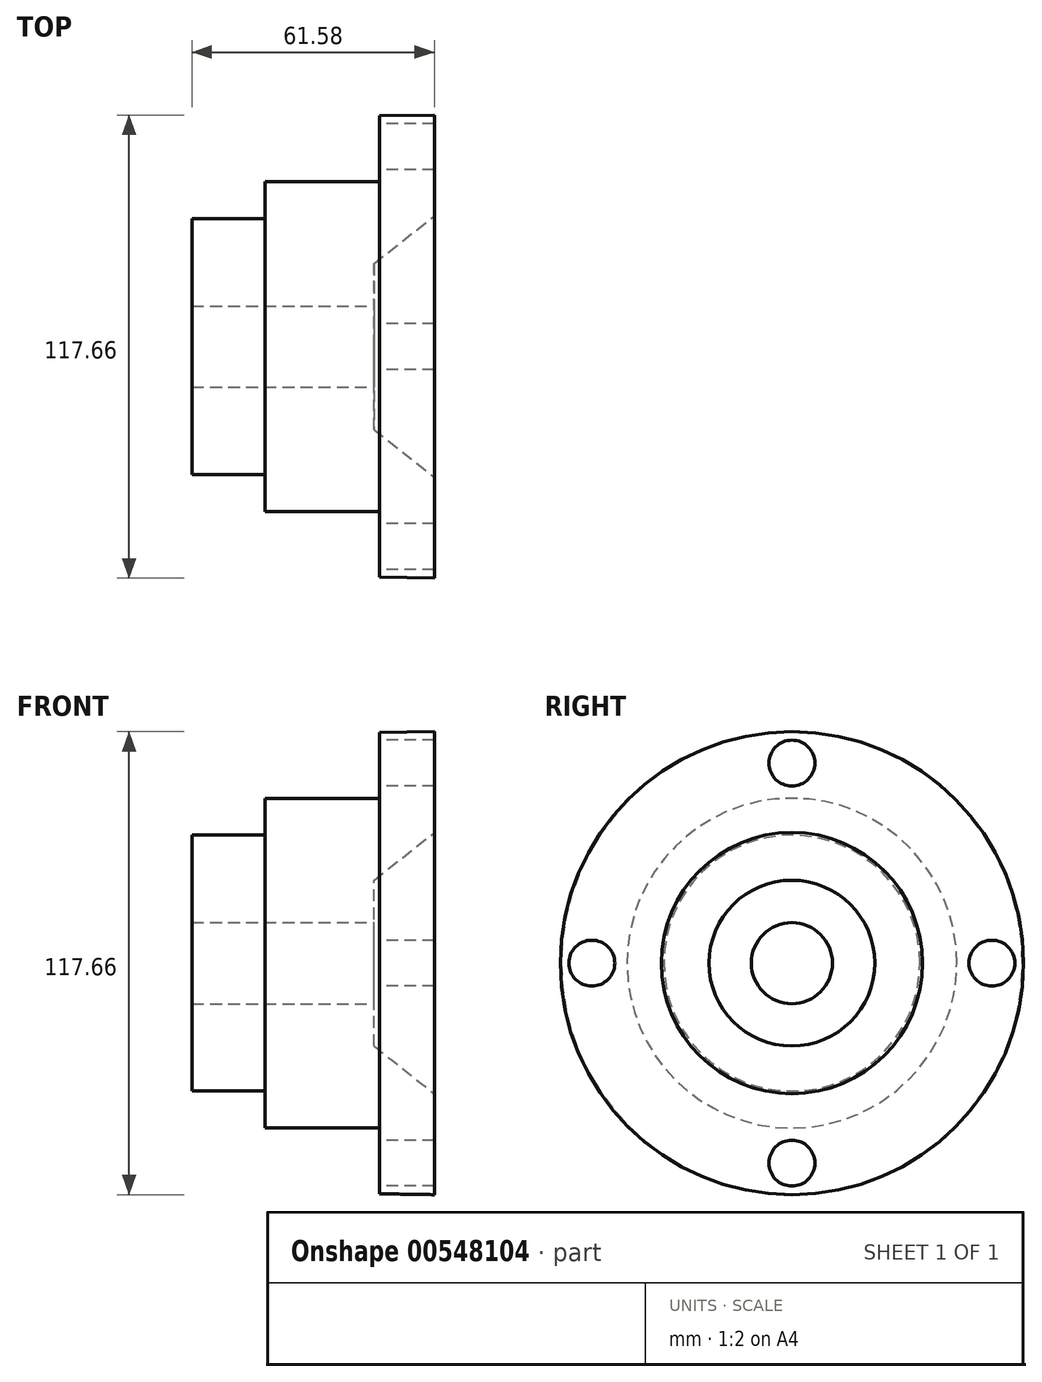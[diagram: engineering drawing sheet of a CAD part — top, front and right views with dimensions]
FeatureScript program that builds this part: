
annotation { "Feature Type Name" : "Feature", "Feature Type Description" : "" }
export const myFeature = defineFeature(function(context is Context, id is Id, definition is map)
    precondition{}
    {
        {
            var Q0;
            Q0=qCreatedBy(makeId("Front.planeOp"),FACE);
            var sketch = newSketch(context, id + "F0", { "sketchPlane" : qUnion([Q0])});
            skLineSegment(sketch, "E0", {"start": v(24.04, 58.83) * mm, "end": v(24.04, 33.2) * mm});
            skLineSegment(sketch, "E1", {"start": v(24.04, 33.2) * mm, "end": v(8.7, 21.06) * mm});
            skLineSegment(sketch, "E2", {"start": v(8.7, 21.06) * mm, "end": v(8.7, 10.3) * mm});
            skLineSegment(sketch, "E3", {"start": v(8.7, 10.3) * mm, "end": v(-37.54, 10.3) * mm});
            skLineSegment(sketch, "E4", {"start": v(-37.54, 10.3) * mm, "end": v(-37.54, 32.5) * mm});
            skLineSegment(sketch, "E5", {"start": v(-37.54, 32.5) * mm, "end": v(-19, 32.5) * mm});
            skLineSegment(sketch, "E6", {"start": v(-19, 32.5) * mm, "end": v(-19, 41.9) * mm});
            skLineSegment(sketch, "E7", {"start": v(-19, 41.9) * mm, "end": v(10.07, 41.9) * mm});
            skLineSegment(sketch, "E8", {"start": v(10.07, 41.9) * mm, "end": v(10.07, 58.6) * mm});
            skLineSegment(sketch, "E9", {"start": v(10.07, 58.6) * mm, "end": v(24.04, 58.83) * mm});
            skLineSegment(sketch, "E10", {"start": v(0, 0) * mm, "end": v(-77.83, 0) * mm});
            skSolve(sketch);
        }
        {
            var Q0;
            Q0 = qSketchRegion(id + "F0", true);
            var Q1;
            Q1=sQuery(id+"F0.wireOp",EDGE,"E10");
            revolve(context, id + "F1", {"entities" : qUnion([Q0]), "axis" : qUnion([Q1]), "revolveType" : RevolveType.FULL});
        }
        {
            var Q0;
            Q0=makeQuery(id+"F1.opRevolve","SWEPT_FACE",FACE,{"disambiguationData":[OSD([sQuery(id+"F0.wireOp",EDGE,"E8")])]});
            var sketch = newSketch(context, id + "F2", { "sketchPlane" : qUnion([Q0])});
            skLineSegment(sketch, "E11", {"start": v(0, 0) * mm, "end": v(0, 71.2) * mm, "construction": true});
            skCircle(sketch, "E12", {"center": v(0, 50.82) * mm, "radius": 5.83 * mm});
            skCircle(sketch, "E13.1.0", {"center": v(-50.82, 0) * mm, "radius": 5.83 * mm});
            skCircle(sketch, "E13.2.0", {"center": v(0, -50.82) * mm, "radius": 5.83 * mm});
            skCircle(sketch, "E13.3.0", {"center": v(50.82, 0) * mm, "radius": 5.83 * mm});
            skPoint(sketch, "E13.center", {"position": v(0, 0) * mm});
            skSolve(sketch);
        }
        {
            var Q0;
            Q0 = qSketchRegion(id + "F2", true);
            extrude(context, id + "F3", {"entities" : qUnion([Q0]), "operationType" : NewBodyOperationType.REMOVE, "oppositeDirection" : true, "depth" : 25 * mm, "offsetDistance" : 25 * mm});
        }
    });
